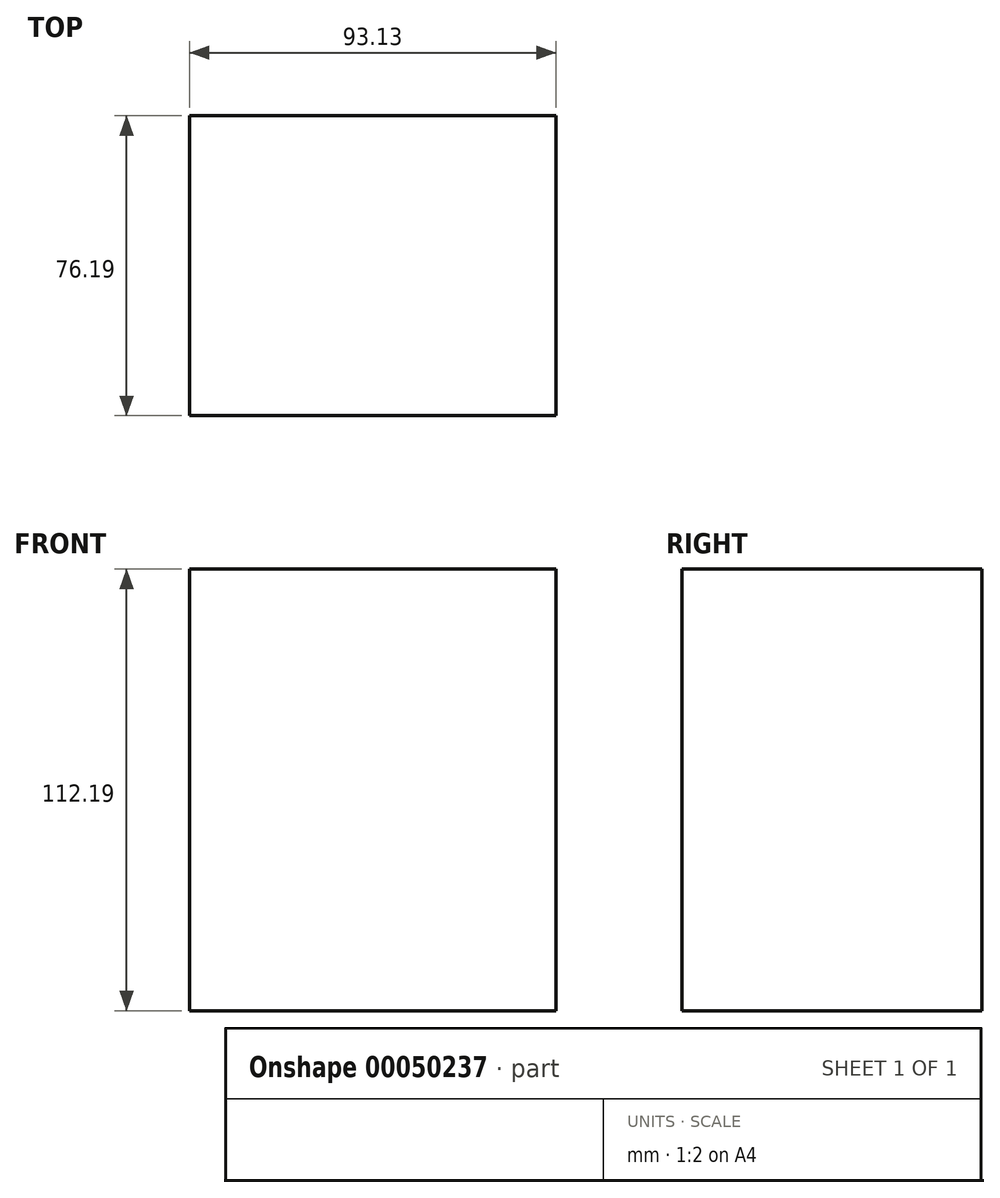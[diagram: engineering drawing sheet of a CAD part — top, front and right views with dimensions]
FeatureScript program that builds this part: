
annotation { "Feature Type Name" : "Feature", "Feature Type Description" : "" }
export const myFeature = defineFeature(function(context is Context, id is Id, definition is map)
    precondition{}
    {
        {
            var Q0;
            Q0=qCreatedBy(makeId("Front.planeOp"),FACE);
            var sketch = newSketch(context, id + "F0", { "sketchPlane" : qUnion([Q0])});
            skLineSegment(sketch, "E0.bottom", {"start": v(-47.44, 55.9) * mm, "end": v(45.7, 55.9) * mm});
            skLineSegment(sketch, "E0.top", {"start": v(-47.44, -56.29) * mm, "end": v(45.7, -56.29) * mm});
            skLineSegment(sketch, "E0.left", {"start": v(-47.44, 55.9) * mm, "end": v(-47.44, -56.29) * mm});
            skLineSegment(sketch, "E0.right", {"start": v(45.7, 55.9) * mm, "end": v(45.7, -56.29) * mm});
            skSolve(sketch);
        }
        {
            var Q0;
            Q0=makeQuery(id+"F0.imprint","IMPRINT",FACE,{"disambiguationData":[TD([[makeQuery(id+"F0.imprint","IMPRINT",EDGE,{"derivedFrom":sQuery(id+"F0.wireOp",EDGE,"E0.bottom")}),-1.0]])]});
            extrude(context, id + "F1", {"entities" : qUnion([Q0]), "depth" : 76.19 * mm});
        }
    });
